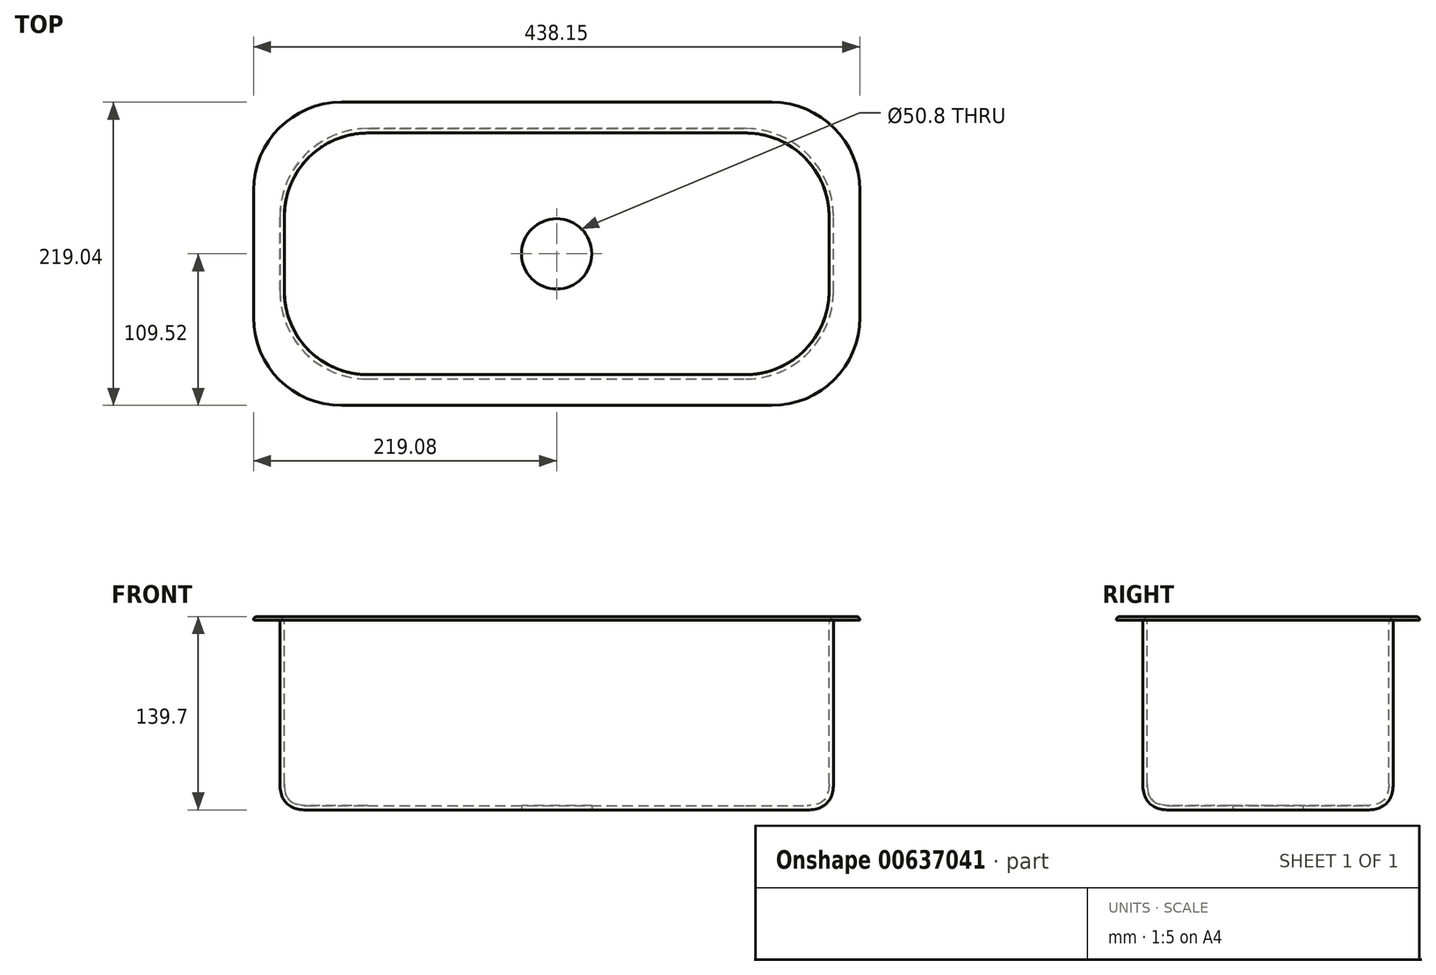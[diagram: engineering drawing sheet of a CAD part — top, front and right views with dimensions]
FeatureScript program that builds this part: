
annotation { "Feature Type Name" : "Feature", "Feature Type Description" : "" }
export const myFeature = defineFeature(function(context is Context, id is Id, definition is map)
    precondition{}
    {
        {
            var Q0;
            Q0=qCreatedBy(makeId("Top.planeOp"),FACE);
            var sketch = newSketch(context, id + "F0", { "sketchPlane" : qUnion([Q0])});
            skLineSegment(sketch, "E0.bottom", {"start": v(136.53, 90.47) * mm, "end": v(-136.53, 90.47) * mm});
            skLineSegment(sketch, "E0.top", {"start": v(136.53, -90.47) * mm, "end": v(-136.53, -90.47) * mm});
            skLineSegment(sketch, "E0.left", {"start": v(200.03, 26.97) * mm, "end": v(200.03, -26.97) * mm});
            skLineSegment(sketch, "E0.right", {"start": v(-200.03, 26.97) * mm, "end": v(-200.03, -26.97) * mm});
            skPoint(sketch, "E0.middle", {"position": v(0, 0) * mm});
            skPoint(sketch, "E1.visualSharp", {"position": v(-200.03, 90.47) * mm});
            skArc(sketch, "E1.filletArc", {"start": v(-136.53, 90.47) * mm, "mid": v(-181.43, 71.88) * mm, "end": v(-200.03, 26.97) * mm});
            skPoint(sketch, "E2.visualSharp", {"position": v(-200.03, -90.47) * mm});
            skArc(sketch, "E2.filletArc", {"start": v(-200.03, -26.97) * mm, "mid": v(-181.43, -71.88) * mm, "end": v(-136.53, -90.47) * mm});
            skPoint(sketch, "E3.visualSharp", {"position": v(200.03, 90.47) * mm});
            skArc(sketch, "E3.filletArc", {"start": v(200.03, 26.97) * mm, "mid": v(181.43, 71.88) * mm, "end": v(136.53, 90.47) * mm});
            skPoint(sketch, "E4.visualSharp", {"position": v(200.03, -90.47) * mm});
            skArc(sketch, "E4.filletArc", {"start": v(136.53, -90.47) * mm, "mid": v(181.43, -71.88) * mm, "end": v(200.03, -26.97) * mm});
            skSolve(sketch);
        }
        {
            var Q0;
            Q0 = qSketchRegion(id + "F0", true);
            extrude(context, id + "F1", {"entities" : qUnion([Q0]), "oppositeDirection" : true, "depth" : 139.7 * mm, "offsetDistance" : 25.4 * mm});
        }
        {
            var Q0;
            Q0=qCreatedBy(makeId("Top.planeOp"),FACE);
            cPlane(context, id + "F2", {"entities" : qUnion([Q0]), "cplaneType" : CPlaneType.OFFSET, "offset" : 139.7 * mm, "oppositeDirection" : true, "width" : 152.4 * mm, "height" : 152.4 * mm});
        }
        {
            var Q0;
            Q0=qCreatedBy(makeId("Top.planeOp"),FACE);
            var sketch = newSketch(context, id + "F3", { "sketchPlane" : qUnion([Q0])});
            skLineSegment(sketch, "E5.bottom", {"start": v(155.58, 109.52) * mm, "end": v(-155.58, 109.52) * mm});
            skLineSegment(sketch, "E5.top", {"start": v(155.58, -109.52) * mm, "end": v(-155.58, -109.52) * mm});
            skLineSegment(sketch, "E5.left", {"start": v(219.08, 46.02) * mm, "end": v(219.08, -46.02) * mm});
            skLineSegment(sketch, "E5.right", {"start": v(-219.08, 46.02) * mm, "end": v(-219.08, -46.02) * mm});
            skPoint(sketch, "E5.middle", {"position": v(0, 0) * mm});
            skPoint(sketch, "E6.visualSharp", {"position": v(219.08, 109.52) * mm});
            skArc(sketch, "E6.filletArc", {"start": v(219.08, 46.02) * mm, "mid": v(200.48, 90.93) * mm, "end": v(155.58, 109.52) * mm});
            skPoint(sketch, "E7.visualSharp", {"position": v(219.08, -109.52) * mm});
            skArc(sketch, "E7.filletArc", {"start": v(155.58, -109.52) * mm, "mid": v(200.48, -90.93) * mm, "end": v(219.08, -46.02) * mm});
            skPoint(sketch, "E8.visualSharp", {"position": v(-219.08, 109.52) * mm});
            skArc(sketch, "E8.filletArc", {"start": v(-155.58, 109.52) * mm, "mid": v(-200.48, 90.93) * mm, "end": v(-219.08, 46.02) * mm});
            skPoint(sketch, "E9.visualSharp", {"position": v(-219.08, -109.52) * mm});
            skArc(sketch, "E9.filletArc", {"start": v(-219.08, -46.02) * mm, "mid": v(-200.48, -90.93) * mm, "end": v(-155.58, -109.52) * mm});
            skSolve(sketch);
        }
        {
            var Q0;
            Q0=makeQuery(id+"F1.opExtrude","CAP_FACE",FACE,{"disambiguationData":[OSD([sQuery(id+"F0.wireOp",EDGE,"E0.bottom"),sQuery(id+"F0.wireOp",EDGE,"E0.top"),sQuery(id+"F0.wireOp",EDGE,"E0.left"),sQuery(id+"F0.wireOp",EDGE,"E0.right"),sQuery(id+"F0.wireOp",EDGE,"E1.filletArc"),sQuery(id+"F0.wireOp",EDGE,"E2.filletArc"),sQuery(id+"F0.wireOp",EDGE,"E3.filletArc"),sQuery(id+"F0.wireOp",EDGE,"E4.filletArc")])],"isStart":false});
            fillet(context, id + "F4", {"entities" : qUnion([Q0]), "radius" : 19.05 * mm, "tangentPropagation" : true, "rho" : 0.5, "crossSection" : FilletCrossSection.CONIC, "allowEdgeOverflow" : false});
        }
        {
            var Q0;
            Q0 = qSketchRegion(id + "F3", true);
            extrude(context, id + "F5", {"entities" : qUnion([Q0]), "operationType" : NewBodyOperationType.ADD, "oppositeDirection" : true, "depth" : 2.54 * mm, "offsetDistance" : 25.4 * mm});
        }
        {
            var Q0;
            Q0=makeQuery(id+"F1.opExtrude","CAP_FACE",FACE,{"disambiguationData":[OSD([sQuery(id+"F0.wireOp",EDGE,"E0.bottom"),sQuery(id+"F0.wireOp",EDGE,"E0.top"),sQuery(id+"F0.wireOp",EDGE,"E0.left"),sQuery(id+"F0.wireOp",EDGE,"E0.right"),sQuery(id+"F0.wireOp",EDGE,"E1.filletArc"),sQuery(id+"F0.wireOp",EDGE,"E2.filletArc"),sQuery(id+"F0.wireOp",EDGE,"E3.filletArc"),sQuery(id+"F0.wireOp",EDGE,"E4.filletArc")])],"isStart":true});
            shell(context, id + "F6", {"entities" : qUnion([Q0]), "thickness" : 3.17 * mm});
        }
        {
            var Q0;
            Q0=qCreatedBy(id+"F2.planeOp",FACE);
            var sketch = newSketch(context, id + "F7", { "sketchPlane" : qUnion([Q0])});
            skCircle(sketch, "E10", {"center": v(0, 0) * mm, "radius": 25.4 * mm});
            skSolve(sketch);
        }
        {
            var Q0;
            Q0 = qSketchRegion(id + "F7", true);
            extrude(context, id + "F8", {"entities" : qUnion([Q0]), "operationType" : NewBodyOperationType.REMOVE, "endBound" : BoundingType.THROUGH_ALL, "depth" : 25.4 * mm, "offsetDistance" : 25.4 * mm});
        }
        {
            var Q0;
            {var subQ0=sQuery(id+"F0.wireOp",EDGE,"E0.bottom");Q0=makeQuery(id+"F6.opShell","TWEAK_EDGE",EDGE,{"derivedFrom":[makeQuery(id+"F5.boolean.opBoolean","MERGE",FACE,{"derivedFrom":[makeQuery(id+"F1.opExtrude","CAP_FACE",FACE,{"disambiguationData":[OSD([subQ0,sQuery(id+"F0.wireOp",EDGE,"E0.top"),sQuery(id+"F0.wireOp",EDGE,"E0.left"),sQuery(id+"F0.wireOp",EDGE,"E0.right"),sQuery(id+"F0.wireOp",EDGE,"E1.filletArc"),sQuery(id+"F0.wireOp",EDGE,"E2.filletArc"),sQuery(id+"F0.wireOp",EDGE,"E3.filletArc"),sQuery(id+"F0.wireOp",EDGE,"E4.filletArc")])],"isStart":true}),makeQuery(id+"F5.opExtrude","CAP_FACE",FACE,{"disambiguationData":[OSD([sQuery(id+"F3.wireOp",EDGE,"E5.bottom"),sQuery(id+"F3.wireOp",EDGE,"E5.top"),sQuery(id+"F3.wireOp",EDGE,"E5.left"),sQuery(id+"F3.wireOp",EDGE,"E5.right"),sQuery(id+"F3.wireOp",EDGE,"E6.filletArc"),sQuery(id+"F3.wireOp",EDGE,"E7.filletArc"),sQuery(id+"F3.wireOp",EDGE,"E8.filletArc"),sQuery(id+"F3.wireOp",EDGE,"E9.filletArc")])],"isStart":true})]}),makeQuery(id+"F1.opExtrude","SWEPT_FACE",FACE,{"disambiguationData":[OSD([subQ0])]})]});}
            fillet(context, id + "F9", {"entities" : qUnion([Q0]), "radius" : 5.08 * mm, "tangentPropagation" : true, "allowEdgeOverflow" : false});
        }
        {
            var Q0;
            Q0=makeQuery(id+"F5.opExtrude","CAP_EDGE",EDGE,{"disambiguationData":[OSD([sQuery(id+"F3.wireOp",EDGE,"E5.top")])],"isStart":true});
            fillet(context, id + "F10", {"entities" : qUnion([Q0]), "radius" : 2.54 * mm, "tangentPropagation" : true, "allowEdgeOverflow" : false});
        }
    });
